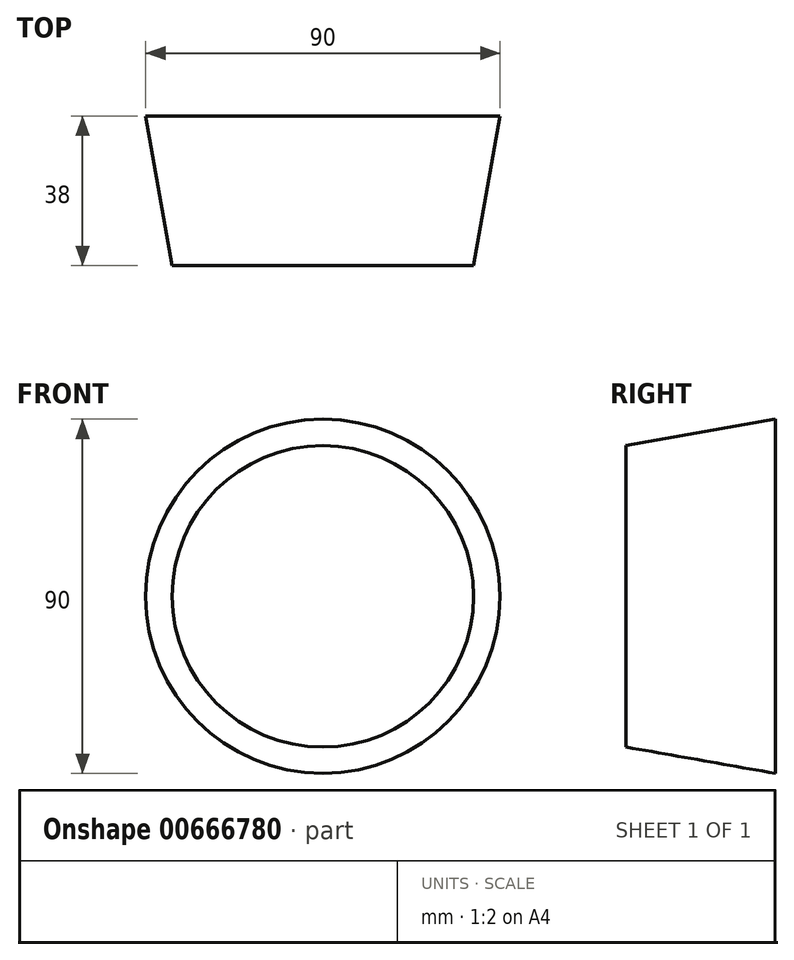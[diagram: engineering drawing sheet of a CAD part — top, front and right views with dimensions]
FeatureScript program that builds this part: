
annotation { "Feature Type Name" : "Feature", "Feature Type Description" : "" }
export const myFeature = defineFeature(function(context is Context, id is Id, definition is map)
    precondition{}
    {
        {
            var Q0;
            Q0=qCreatedBy(makeId("Front.planeOp"),FACE);
            var sketch = newSketch(context, id + "F0", { "sketchPlane" : qUnion([Q0])});
            skCircle(sketch, "E0", {"center": v(0, 0) * mm, "radius": 45 * mm});
            skSolve(sketch);
        }
        {
            var Q0;
            Q0 = qSketchRegion(id + "F0", true);
            extrude(context, id + "F1", {"entities" : qUnion([Q0]), "depth" : 38 * mm, "offsetDistance" : 25 * mm, "hasDraft" : true, "draftAngle" : 10 * degree, "draftPullDirection" : true});
        }
    });
